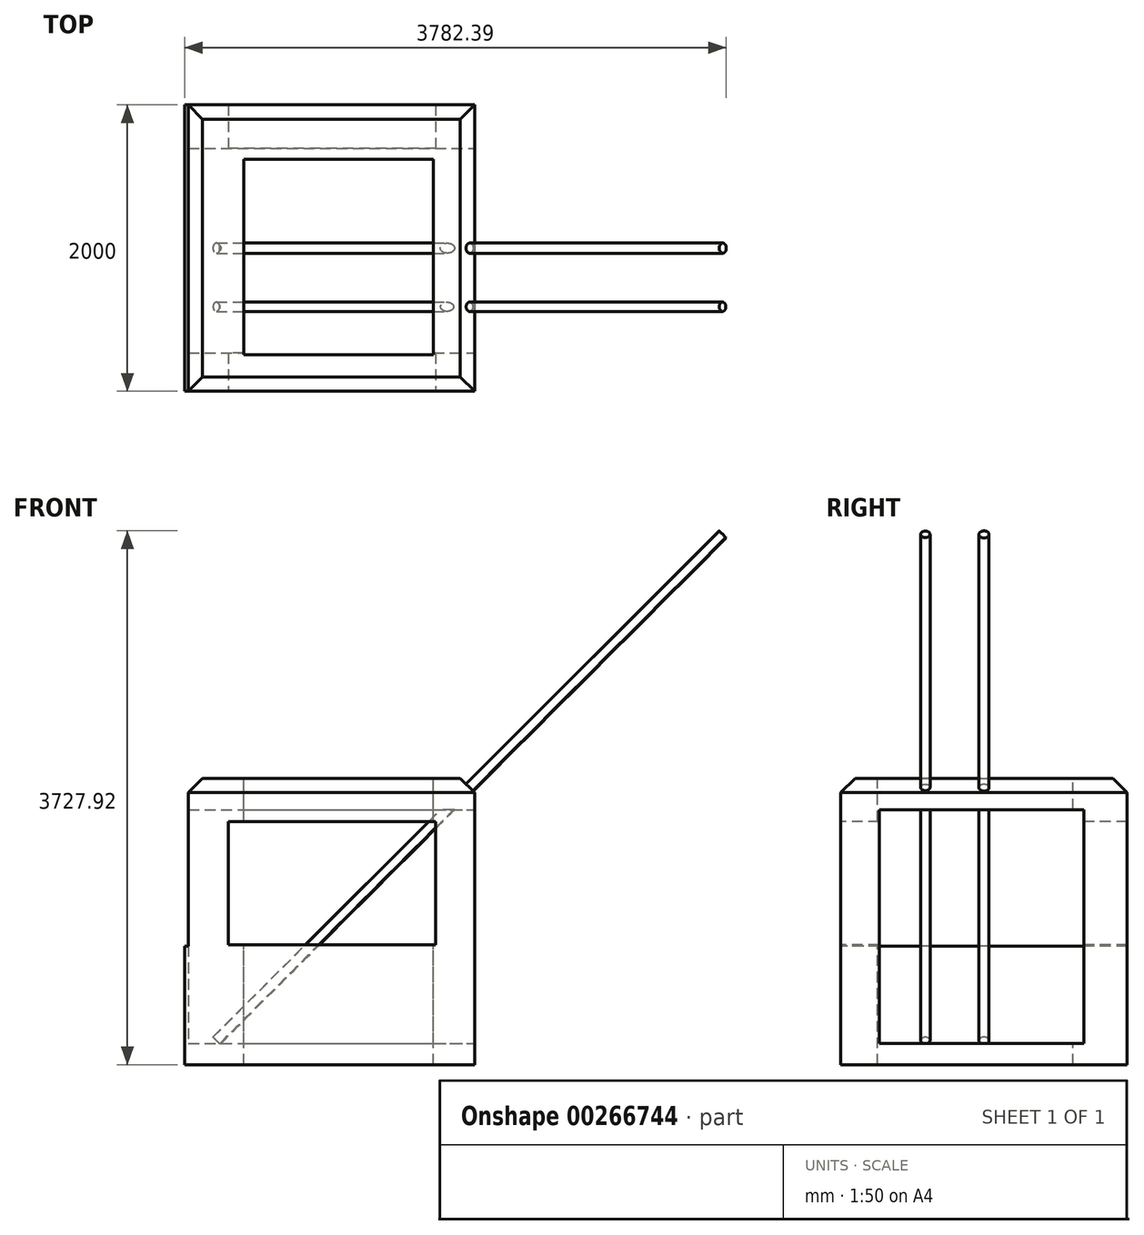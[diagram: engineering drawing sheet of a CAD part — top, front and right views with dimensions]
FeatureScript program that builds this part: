
annotation { "Feature Type Name" : "Feature", "Feature Type Description" : "" }
export const myFeature = defineFeature(function(context is Context, id is Id, definition is map)
    precondition{}
    {
        {
            var Q0;
            Q0=qCreatedBy(makeId("Front.planeOp"),FACE);
            var sketch = newSketch(context, id + "F0", { "sketchPlane" : qUnion([Q0])});
            skLineSegment(sketch, "E0.bottom", {"start": v(-88.94, 2000) * mm, "end": v(1911.06, 2000) * mm});
            skLineSegment(sketch, "E0.top", {"start": v(-88.94, 0) * mm, "end": v(1911.06, 0) * mm});
            skLineSegment(sketch, "E0.left", {"start": v(-88.94, 2000) * mm, "end": v(-88.94, 0) * mm});
            skLineSegment(sketch, "E0.right", {"start": v(1911.06, 2000) * mm, "end": v(1911.06, 0) * mm});
            skSolve(sketch);
        }
        {
            var Q0;
            Q0 = qSketchRegion(id + "F0", true);
            extrude(context, id + "F1", {"entities" : qUnion([Q0]), "depth" : 2000 * mm});
        }
        {
            var Q0;
            Q0=makeQuery(id+"F1.opExtrude","CAP_FACE",FACE,{"disambiguationData":[OSD([sQuery(id+"F0.wireOp",EDGE,"E0.bottom"),sQuery(id+"F0.wireOp",EDGE,"E0.top"),sQuery(id+"F0.wireOp",EDGE,"E0.left"),sQuery(id+"F0.wireOp",EDGE,"E0.right")])],"isStart":false});
            var sketch = newSketch(context, id + "F2", { "sketchPlane" : qUnion([Q0])});
            skLineSegment(sketch, "E1.bottom", {"start": v(191.56, 1698.75) * mm, "end": v(1639.21, 1698.75) * mm});
            skLineSegment(sketch, "E1.top", {"start": v(191.56, 837.1) * mm, "end": v(1639.21, 837.1) * mm});
            skLineSegment(sketch, "E1.left", {"start": v(191.56, 1698.75) * mm, "end": v(191.56, 837.1) * mm});
            skLineSegment(sketch, "E1.right", {"start": v(1639.21, 1698.75) * mm, "end": v(1639.21, 837.1) * mm});
            skSolve(sketch);
        }
        {
            var Q0;
            Q0=makeQuery(id+"F2.imprint","IMPRINT",FACE,{"disambiguationData":[TD([[makeQuery(id+"F2.imprint","IMPRINT",EDGE,{"derivedFrom":sQuery(id+"F2.wireOp",EDGE,"E1.bottom")}),-1.0]])]});
            extrude(context, id + "F3", {"entities" : qUnion([Q0]), "operationType" : NewBodyOperationType.REMOVE, "endBound" : BoundingType.THROUGH_ALL, "oppositeDirection" : true, "depth" : 25 * mm});
        }
        {
            var Q0;
            Q0=makeQuery(id+"F1.opExtrude","SWEPT_FACE",FACE,{"disambiguationData":[OSD([sQuery(id+"F0.wireOp",EDGE,"E0.bottom")])]});
            var sketch = newSketch(context, id + "F4", { "sketchPlane" : qUnion([Q0])});
            skLineSegment(sketch, "E2.bottom", {"start": v(298.07, -379.84) * mm, "end": v(1622.91, -379.84) * mm});
            skLineSegment(sketch, "E2.top", {"start": v(298.07, -1743.62) * mm, "end": v(1622.91, -1743.62) * mm});
            skLineSegment(sketch, "E2.left", {"start": v(298.07, -379.84) * mm, "end": v(298.07, -1743.62) * mm});
            skLineSegment(sketch, "E2.right", {"start": v(1622.91, -379.84) * mm, "end": v(1622.91, -1743.62) * mm});
            skSolve(sketch);
        }
        {
            var Q0;
            Q0 = qSketchRegion(id + "F4", true);
            extrude(context, id + "F5", {"entities" : qUnion([Q0]), "operationType" : NewBodyOperationType.REMOVE, "endBound" : BoundingType.THROUGH_ALL, "oppositeDirection" : true, "depth" : 25 * mm});
        }
        {
            var Q0;
            Q0=makeQuery(id+"F1.opExtrude","SWEPT_FACE",FACE,{"disambiguationData":[OSD([sQuery(id+"F0.wireOp",EDGE,"E0.right")])]});
            var sketch = newSketch(context, id + "F6", { "sketchPlane" : qUnion([Q0])});
            skLineSegment(sketch, "E3.bottom", {"start": v(-1732.77, 1780.44) * mm, "end": v(-303.27, 1780.44) * mm});
            skLineSegment(sketch, "E3.top", {"start": v(-1732.77, 148.1) * mm, "end": v(-303.27, 148.1) * mm});
            skLineSegment(sketch, "E3.left", {"start": v(-1732.77, 1780.44) * mm, "end": v(-1732.77, 148.1) * mm});
            skLineSegment(sketch, "E3.right", {"start": v(-303.27, 1780.44) * mm, "end": v(-303.27, 148.1) * mm});
            skSolve(sketch);
        }
        {
            var Q0;
            Q0 = qSketchRegion(id + "F6", true);
            extrude(context, id + "F7", {"entities" : qUnion([Q0]), "operationType" : NewBodyOperationType.REMOVE, "endBound" : BoundingType.THROUGH_ALL, "oppositeDirection" : true, "depth" : 25 * mm});
        }
        {
            var Q0;
            Q0=makeQuery(id+"F1.opExtrude","SWEPT_EDGE",EDGE,{"disambiguationData":[OSD([sQuery(id+"F0.wireOp",EDGE,"E0.bottom"),sQuery(id+"F0.wireOp",EDGE,"E0.right")])]});
            var Q1;
            Q1=makeQuery(id+"F1.opExtrude","CAP_EDGE",EDGE,{"disambiguationData":[OSD([sQuery(id+"F0.wireOp",EDGE,"E0.bottom")])],"isStart":true});
            var Q2;
            Q2=makeQuery(id+"F1.opExtrude","CAP_EDGE",EDGE,{"disambiguationData":[OSD([sQuery(id+"F0.wireOp",EDGE,"E0.bottom")])],"isStart":false});
            var Q3;
            Q3=makeQuery(id+"F1.opExtrude","SWEPT_EDGE",EDGE,{"disambiguationData":[OSD([sQuery(id+"F0.wireOp",EDGE,"E0.bottom"),sQuery(id+"F0.wireOp",EDGE,"E0.left")])]});
            var Q4;
            Q4=makeQuery(id+"F5.boolean.opBoolean","COPY",EDGE,{"derivedFrom":makeQuery(id+"F5.opExtrude","CAP_EDGE",EDGE,{"disambiguationData":[OSD([sQuery(id+"F4.wireOp",EDGE,"E2.left")])],"isStart":true})});
            var Q5;
            Q5=makeQuery(id+"F5.boolean.opBoolean","COPY",EDGE,{"derivedFrom":makeQuery(id+"F5.opExtrude","CAP_EDGE",EDGE,{"disambiguationData":[OSD([sQuery(id+"F4.wireOp",EDGE,"E2.right")])],"isStart":true})});
            chamfer(context, id + "F8", {"entities" : qUnion([Q0, Q1, Q2, Q3, Q4, Q5]), "width" : 100 * mm, "tangentPropagation" : true});
        }
        {
            var Q0;
            Q0=makeQuery(id+"F1.opExtrude","SWEPT_FACE",FACE,{"disambiguationData":[OSD([sQuery(id+"F0.wireOp",EDGE,"E0.left")])]});
            var sketch = newSketch(context, id + "F9", { "sketchPlane" : qUnion([Q0])});
            skLineSegment(sketch, "E4.bottom", {"start": v(0, 828.46) * mm, "end": v(2000, 828.46) * mm});
            skLineSegment(sketch, "E4.top", {"start": v(0, 0) * mm, "end": v(2000, 0) * mm});
            skLineSegment(sketch, "E4.left", {"start": v(0, 828.46) * mm, "end": v(0, 0) * mm});
            skLineSegment(sketch, "E4.right", {"start": v(2000, 828.46) * mm, "end": v(2000, 0) * mm});
            skSolve(sketch);
        }
        {
            var Q0;
            Q0 = qSketchRegion(id + "F9", true);
            extrude(context, id + "F10", {"entities" : qUnion([Q0]), "operationType" : NewBodyOperationType.ADD, "depth" : 25 * mm});
        }
        {
            var Q0;
            Q0=makeQuery(id+"F8.opChamfer","BLEND_FACE",FACE,{"disambiguationData":[OSD([sQuery(id+"F0.wireOp",EDGE,"E0.bottom"),sQuery(id+"F0.wireOp",EDGE,"E0.right")])]});
            var sketch = newSketch(context, id + "F11", { "sketchPlane" : qUnion([Q0])});
            skCircle(sketch, "E5", {"center": v(-1409.59, 43.84) * mm, "radius": 32.3 * mm});
            skCircle(sketch, "E6", {"center": v(-1000.06, 42.05) * mm, "radius": 35.2 * mm});
            skSolve(sketch);
        }
        {
            var Q0;
            Q0 = qSketchRegion(id + "F11", true);
            extrude(context, id + "F12", {"entities" : qUnion([Q0]), "operationType" : NewBodyOperationType.ADD, "endBound" : BoundingType.SYMMETRIC, "oppositeDirection" : true, "depth" : 5000 * mm});
        }
    });
